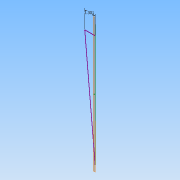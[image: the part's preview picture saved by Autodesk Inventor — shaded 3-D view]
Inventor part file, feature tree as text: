
AUTODESK INVENTOR PART (.ipt)
format: ipt  version: 2013 (Build 170138000, 138)  size: 57,344 bytes
history: native  units: in
note: dims shown in document units (in); Inventor stores cm internally (conversion verified against a paired STEP export)
features: plane x1, sketch x1, reference x1
ambient origin geometry x8: Origin, YZ Plane, XZ Plane, XY Plane, X Axis, Y Axis, Z Axis, Center Point
feature tree (3):
  plane  "Work Plane1"
  sketch  "Sketch1"  dims[d0=3.3013in]
  reference  "Reference1"
